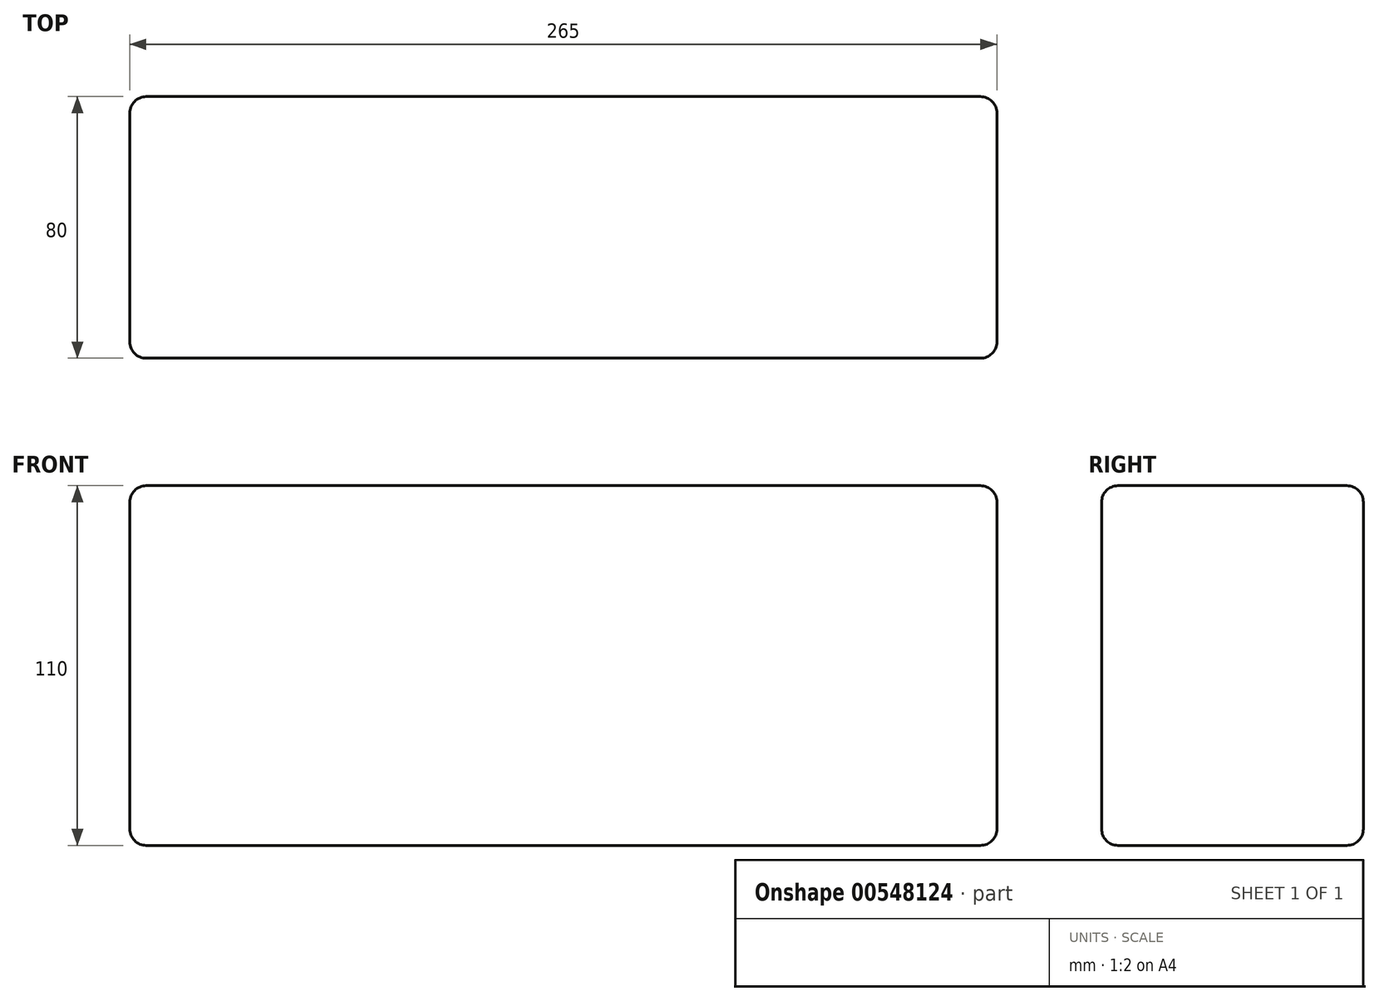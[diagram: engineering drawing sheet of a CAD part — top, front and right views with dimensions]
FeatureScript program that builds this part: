
annotation { "Feature Type Name" : "Feature", "Feature Type Description" : "" }
export const myFeature = defineFeature(function(context is Context, id is Id, definition is map)
    precondition{}
    {
        {
            var Q0;
            Q0=qCreatedBy(makeId("Top.planeOp"),FACE);
            var sketch = newSketch(context, id + "F0", { "sketchPlane" : qUnion([Q0])});
            skLineSegment(sketch, "E0.bottom", {"start": v(0, 0) * mm, "end": v(-265, 0) * mm});
            skLineSegment(sketch, "E0.top", {"start": v(0, 80) * mm, "end": v(-265, 80) * mm});
            skLineSegment(sketch, "E0.left", {"start": v(0, 0) * mm, "end": v(0, 80) * mm});
            skLineSegment(sketch, "E0.right", {"start": v(-265, 0) * mm, "end": v(-265, 80) * mm});
            skSolve(sketch);
        }
        {
            var Q0;
            Q0=makeQuery(id+"F0.imprint","IMPRINT",FACE,{"disambiguationData":[TD([[makeQuery(id+"F0.imprint","IMPRINT",EDGE,{"derivedFrom":sQuery(id+"F0.wireOp",EDGE,"E0.bottom")}),-1.0]])]});
            extrude(context, id + "F1", {"entities" : qUnion([Q0]), "depth" : 110 * mm, "offsetDistance" : 25 * mm});
        }
        {
            var Q0;
            Q0=makeQuery(id+"F1.opExtrude","SWEPT_FACE",FACE,{"disambiguationData":[OSD([sQuery(id+"F0.wireOp",EDGE,"E0.bottom")])]});
            var Q1;
            Q1=makeQuery(id+"F1.opExtrude","CAP_FACE",FACE,{"disambiguationData":[OSD([sQuery(id+"F0.wireOp",EDGE,"E0.bottom"),sQuery(id+"F0.wireOp",EDGE,"E0.top"),sQuery(id+"F0.wireOp",EDGE,"E0.left"),sQuery(id+"F0.wireOp",EDGE,"E0.right")])],"isStart":false});
            var Q2;
            Q2=makeQuery(id+"F1.opExtrude","SWEPT_FACE",FACE,{"disambiguationData":[OSD([sQuery(id+"F0.wireOp",EDGE,"E0.left")])]});
            var Q3;
            Q3=makeQuery(id+"F1.opExtrude","SWEPT_FACE",FACE,{"disambiguationData":[OSD([sQuery(id+"F0.wireOp",EDGE,"E0.right")])]});
            var Q4;
            Q4=makeQuery(id+"F1.opExtrude","SWEPT_FACE",FACE,{"disambiguationData":[OSD([sQuery(id+"F0.wireOp",EDGE,"E0.top")])]});
            var Q5;
            Q5=makeQuery(id+"F1.opExtrude","CAP_FACE",FACE,{"disambiguationData":[OSD([sQuery(id+"F0.wireOp",EDGE,"E0.bottom"),sQuery(id+"F0.wireOp",EDGE,"E0.top"),sQuery(id+"F0.wireOp",EDGE,"E0.left"),sQuery(id+"F0.wireOp",EDGE,"E0.right")])],"isStart":true});
            fillet(context, id + "F2", {"entities" : qUnion([Q0, Q1, Q2, Q3, Q4, Q5]), "radius" : 5 * mm, "tangentPropagation" : true, "allowEdgeOverflow" : false});
        }
    });
